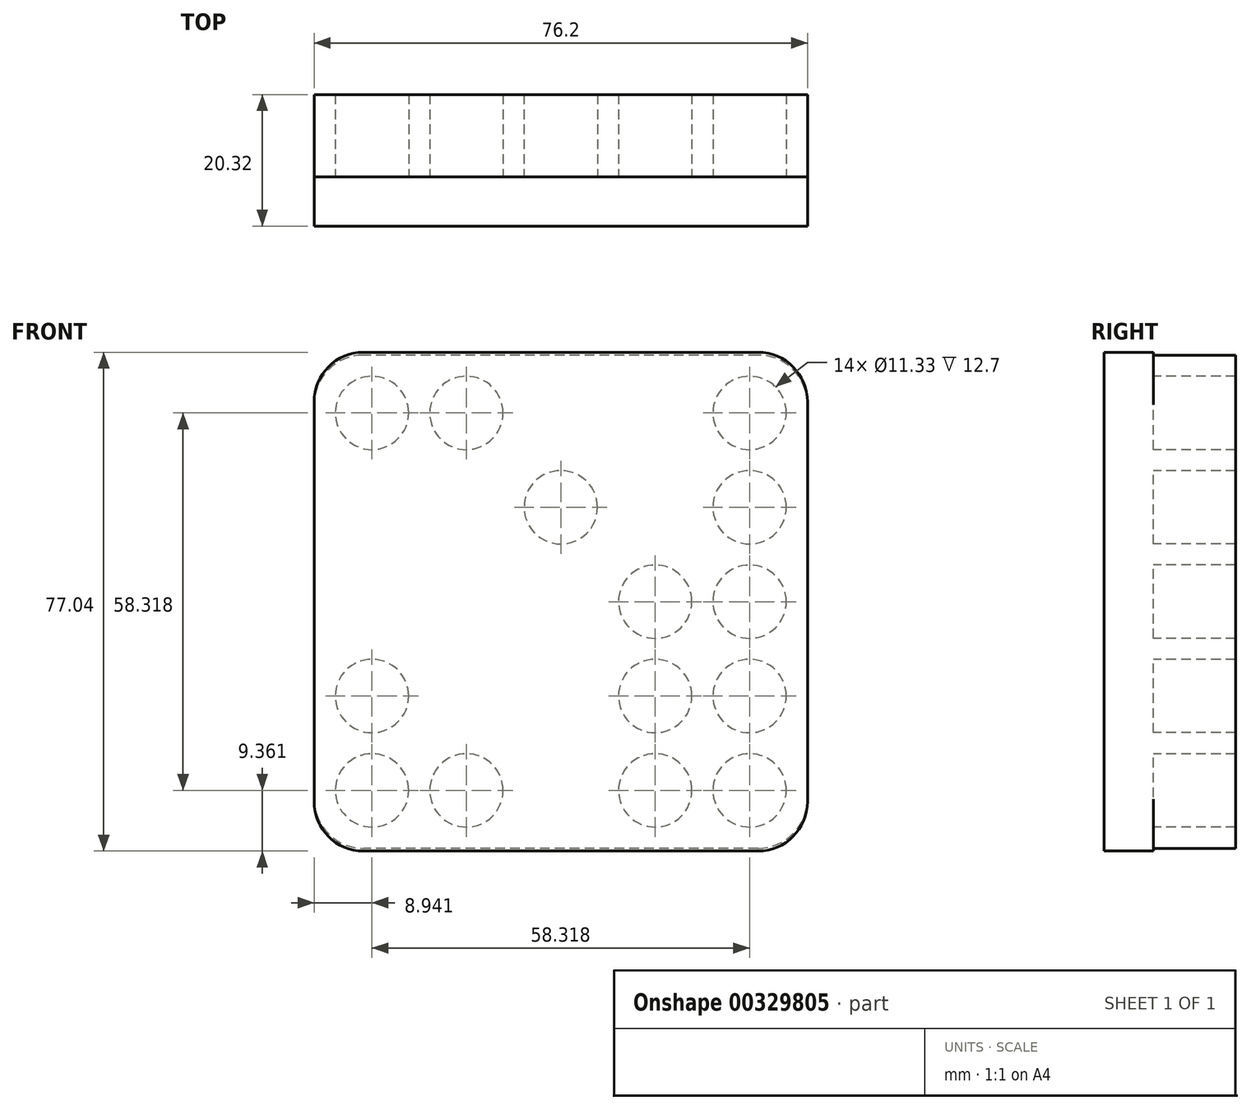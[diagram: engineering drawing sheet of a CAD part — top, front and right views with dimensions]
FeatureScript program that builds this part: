
annotation { "Feature Type Name" : "Feature", "Feature Type Description" : "" }
export const myFeature = defineFeature(function(context is Context, id is Id, definition is map)
    precondition{}
    {
        {
            var Q0;
            Q0=qCreatedBy(makeId("Front.planeOp"),FACE);
            var sketch = newSketch(context, id + "F0", { "sketchPlane" : qUnion([Q0])});
            skLineSegment(sketch, "E0.bottom", {"start": v(38.1, -38.1) * mm, "end": v(-38.1, -38.1) * mm});
            skLineSegment(sketch, "E0.top", {"start": v(38.1, 38.1) * mm, "end": v(-38.1, 38.1) * mm});
            skLineSegment(sketch, "E0.left", {"start": v(38.1, -38.1) * mm, "end": v(38.1, 38.1) * mm});
            skLineSegment(sketch, "E0.right", {"start": v(-38.1, -38.1) * mm, "end": v(-38.1, 38.1) * mm});
            skPoint(sketch, "E0.middle", {"position": v(0, 0) * mm});
            skLineSegment(sketch, "E1.left", {"start": v(38.1, -38.1) * mm, "end": v(38.1, -30.48) * mm});
            skSolve(sketch);
        }
        {
            var Q0;
            Q0 = qSketchRegion(id + "F0", true);
            extrude(context, id + "F1", {"entities" : qUnion([Q0]), "depth" : 12.7 * mm});
        }
        {
            var Q0;
            Q0=makeQuery(id+"F1.opExtrude","CAP_FACE",FACE,{"disambiguationData":[OSD([sQuery(id+"F0.wireOp",EDGE,"E0.bottom"),sQuery(id+"F0.wireOp",EDGE,"E0.top"),sQuery(id+"F0.wireOp",EDGE,"E0.left"),sQuery(id+"F0.wireOp",EDGE,"E0.right"),sQuery(id+"F0.wireOp",EDGE,"jwXeI2Gn-2uBu-UpR7-ZfaP-BlmGfNdsuJBv.bottom"),sQuery(id+"F0.wireOp",EDGE,"jwXeI2Gn-2uBu-UpR7-ZfaP-BlmGfNdsuJBv.top"),sQuery(id+"F0.wireOp",EDGE,"jwXeI2Gn-2uBu-UpR7-ZfaP-BlmGfNdsuJBv.right"),sQuery(id+"F0.wireOp",EDGE,"E1.bottom"),sQuery(id+"F0.wireOp",EDGE,"E1.top"),sQuery(id+"F0.wireOp",EDGE,"E1.right"),sQuery(id+"F0.wireOp",EDGE,"Ah4uGkzg-DGqc-S60Q-QTGu-lLs24q3gFamp.bottom"),sQuery(id+"F0.wireOp",EDGE,"Ah4uGkzg-DGqc-S60Q-QTGu-lLs24q3gFamp.left"),sQuery(id+"F0.wireOp",EDGE,"Ah4uGkzg-DGqc-S60Q-QTGu-lLs24q3gFamp.right")])],"isStart":false});
            var sketch = newSketch(context, id + "F2", { "sketchPlane" : qUnion([Q0])});
            skLineSegment(sketch, "E2.bottom", {"start": v(0, 0) * mm, "end": v(14.58, 0) * mm});
            skLineSegment(sketch, "E2.top", {"start": v(0, 14.58) * mm, "end": v(14.58, 14.58) * mm});
            skLineSegment(sketch, "E2.left", {"start": v(0, 0) * mm, "end": v(0, 14.58) * mm});
            skLineSegment(sketch, "E2.right", {"start": v(14.58, 0) * mm, "end": v(14.58, 14.58) * mm});
            skLineSegment(sketch, "E3.top", {"start": v(0, 29.16) * mm, "end": v(14.58, 29.16) * mm});
            skLineSegment(sketch, "E3.left", {"start": v(0, 14.58) * mm, "end": v(0, 29.16) * mm});
            skLineSegment(sketch, "E3.right", {"start": v(14.58, 14.58) * mm, "end": v(14.58, 29.16) * mm});
            skLineSegment(sketch, "E4.top", {"start": v(0, -14.58) * mm, "end": v(14.58, -14.58) * mm});
            skLineSegment(sketch, "E4.left", {"start": v(0, 0) * mm, "end": v(0, -14.58) * mm});
            skLineSegment(sketch, "E4.right", {"start": v(14.58, 0) * mm, "end": v(14.58, -14.58) * mm});
            skLineSegment(sketch, "E5.bottom", {"start": v(0, 0) * mm, "end": v(-14.58, 0) * mm});
            skLineSegment(sketch, "E5.top", {"start": v(0, -14.58) * mm, "end": v(-14.58, -14.58) * mm});
            skLineSegment(sketch, "E5.right", {"start": v(-14.58, 0) * mm, "end": v(-14.58, -14.58) * mm});
            skLineSegment(sketch, "E6.bottom", {"start": v(0, 14.58) * mm, "end": v(-14.58, 14.58) * mm});
            skLineSegment(sketch, "E6.left", {"start": v(0, 14.58) * mm, "end": v(0, 0) * mm});
            skLineSegment(sketch, "E6.right", {"start": v(-14.58, 14.58) * mm, "end": v(-14.58, 0) * mm});
            skLineSegment(sketch, "E7.top", {"start": v(0, 29.16) * mm, "end": v(-14.58, 29.16) * mm});
            skLineSegment(sketch, "E7.right", {"start": v(-14.58, 14.58) * mm, "end": v(-14.58, 29.16) * mm});
            skLineSegment(sketch, "E8.bottom", {"start": v(-14.58, 14.58) * mm, "end": v(-29.16, 14.58) * mm});
            skLineSegment(sketch, "E8.top", {"start": v(-14.58, 29.16) * mm, "end": v(-29.16, 29.16) * mm});
            skLineSegment(sketch, "E8.right", {"start": v(-29.16, 14.58) * mm, "end": v(-29.16, 29.16) * mm});
            skLineSegment(sketch, "E9.top", {"start": v(-14.58, 0) * mm, "end": v(-29.16, 0) * mm});
            skLineSegment(sketch, "E9.right", {"start": v(-29.16, 14.58) * mm, "end": v(-29.16, 0) * mm});
            skLineSegment(sketch, "E10.bottom", {"start": v(-14.58, -14.58) * mm, "end": v(-29.16, -14.58) * mm});
            skLineSegment(sketch, "E10.left", {"start": v(-14.58, -14.58) * mm, "end": v(-14.58, 0) * mm});
            skLineSegment(sketch, "E10.right", {"start": v(-29.16, -14.58) * mm, "end": v(-29.16, 0) * mm});
            skLineSegment(sketch, "E11.bottom", {"start": v(14.58, -14.58) * mm, "end": v(29.16, -14.58) * mm});
            skLineSegment(sketch, "E11.top", {"start": v(14.58, 0) * mm, "end": v(29.16, 0) * mm});
            skLineSegment(sketch, "E11.left", {"start": v(14.58, -14.58) * mm, "end": v(14.58, 0) * mm});
            skLineSegment(sketch, "E11.right", {"start": v(29.16, -14.58) * mm, "end": v(29.16, 0) * mm});
            skLineSegment(sketch, "E12.top", {"start": v(14.58, 14.58) * mm, "end": v(29.16, 14.58) * mm});
            skLineSegment(sketch, "E12.right", {"start": v(29.16, 0) * mm, "end": v(29.16, 14.58) * mm});
            skLineSegment(sketch, "E13.top", {"start": v(14.58, 29.16) * mm, "end": v(29.16, 29.16) * mm});
            skLineSegment(sketch, "E13.right", {"start": v(29.16, 14.58) * mm, "end": v(29.16, 29.16) * mm});
            skLineSegment(sketch, "E14.top", {"start": v(14.58, -29.16) * mm, "end": v(29.16, -29.16) * mm});
            skLineSegment(sketch, "E14.left", {"start": v(14.58, -14.58) * mm, "end": v(14.58, -29.16) * mm});
            skLineSegment(sketch, "E14.right", {"start": v(29.16, -14.58) * mm, "end": v(29.16, -29.16) * mm});
            skLineSegment(sketch, "E15.bottom", {"start": v(14.58, -29.16) * mm, "end": v(0, -29.16) * mm});
            skLineSegment(sketch, "E15.top", {"start": v(14.58, -14.58) * mm, "end": v(0, -14.58) * mm});
            skLineSegment(sketch, "E15.left", {"start": v(14.58, -29.16) * mm, "end": v(14.58, -14.58) * mm});
            skLineSegment(sketch, "E15.right", {"start": v(0, -29.16) * mm, "end": v(0, -14.58) * mm});
            skLineSegment(sketch, "E16.bottom", {"start": v(0, -29.16) * mm, "end": v(-14.58, -29.16) * mm});
            skLineSegment(sketch, "E16.right", {"start": v(-14.58, -29.16) * mm, "end": v(-14.58, -14.58) * mm});
            skLineSegment(sketch, "E17.bottom", {"start": v(-14.58, -29.16) * mm, "end": v(-29.16, -29.16) * mm});
            skLineSegment(sketch, "E17.right", {"start": v(-29.16, -29.16) * mm, "end": v(-29.16, -14.58) * mm});
            skSolve(sketch);
        }
        {
            var Q0;
            Q0=sQuery(id+"F2.wireOp",VERTEX,"E8.top.end");
            var Q1;
            Q1=sQuery(id+"F2.wireOp",VERTEX,"E8.top.start");
            var Q2;
            Q2=sQuery(id+"F2.wireOp",VERTEX,"E3.left.end");
            var Q3;
            Q3=sQuery(id+"F2.wireOp",VERTEX,"E3.right.end");
            var Q4;
            Q4=sQuery(id+"F2.wireOp",VERTEX,"E13.right.end");
            var Q5;
            Q5=sQuery(id+"F2.wireOp",VERTEX,"E12.top.end");
            var Q6;
            Q6=sQuery(id+"F2.wireOp",VERTEX,"E11.right.end");
            var Q7;
            Q7=sQuery(id+"F2.wireOp",VERTEX,"E11.bottom.end");
            var Q8;
            Q8=sQuery(id+"F2.wireOp",VERTEX,"E14.top.end");
            var Q9;
            Q9=sQuery(id+"F2.wireOp",VERTEX,"E14.top.start");
            var Q10;
            Q10=sQuery(id+"F2.wireOp",VERTEX,"E14.left.start");
            var Q11;
            Q11=sQuery(id+"F2.wireOp",VERTEX,"E11.left.end");
            var Q12;
            Q12=sQuery(id+"F2.wireOp",VERTEX,"E2.top.end");
            var Q13;
            Q13=sQuery(id+"F2.wireOp",VERTEX,"E6.left.start");
            var Q14;
            Q14=sQuery(id+"F2.wireOp",VERTEX,"E2.bottom.start");
            var Q15;
            Q15=sQuery(id+"F2.wireOp",VERTEX,"E4.left.end");
            var Q16;
            Q16=sQuery(id+"F2.wireOp",VERTEX,"E15.right.start");
            var Q17;
            Q17=sQuery(id+"F2.wireOp",VERTEX,"E16.right.start");
            var Q18;
            Q18=sQuery(id+"F2.wireOp",VERTEX,"E16.right.end");
            var Q19;
            Q19=sQuery(id+"F2.wireOp",VERTEX,"E6.right.end");
            var Q20;
            Q20=sQuery(id+"F2.wireOp",VERTEX,"E7.right.start");
            var Q21;
            Q21=sQuery(id+"F2.wireOp",VERTEX,"E8.bottom.end");
            var Q22;
            Q22=sQuery(id+"F2.wireOp",VERTEX,"E9.top.end");
            var Q23;
            Q23=sQuery(id+"F2.wireOp",VERTEX,"E17.right.end");
            var Q24;
            Q24=sQuery(id+"F2.wireOp",VERTEX,"E17.bottom.end");
            var Q25;
            Q25=makeQuery(id+"F1.opExtrude","SWEPT_BODY",BODY,{"disambiguationData":[OSD([sQuery(id+"F0.wireOp",EDGE,"E0.bottom"),sQuery(id+"F0.wireOp",EDGE,"E0.top"),sQuery(id+"F0.wireOp",EDGE,"E0.left"),sQuery(id+"F0.wireOp",EDGE,"E0.right"),sQuery(id+"F0.wireOp",EDGE,"jwXeI2Gn-2uBu-UpR7-ZfaP-BlmGfNdsuJBv.bottom"),sQuery(id+"F0.wireOp",EDGE,"jwXeI2Gn-2uBu-UpR7-ZfaP-BlmGfNdsuJBv.top"),sQuery(id+"F0.wireOp",EDGE,"jwXeI2Gn-2uBu-UpR7-ZfaP-BlmGfNdsuJBv.right"),sQuery(id+"F0.wireOp",EDGE,"E1.bottom"),sQuery(id+"F0.wireOp",EDGE,"E1.top"),sQuery(id+"F0.wireOp",EDGE,"E1.right"),sQuery(id+"F0.wireOp",EDGE,"Ah4uGkzg-DGqc-S60Q-QTGu-lLs24q3gFamp.bottom"),sQuery(id+"F0.wireOp",EDGE,"Ah4uGkzg-DGqc-S60Q-QTGu-lLs24q3gFamp.left"),sQuery(id+"F0.wireOp",EDGE,"Ah4uGkzg-DGqc-S60Q-QTGu-lLs24q3gFamp.right")])]});
            hole(context, id + "F3", {"style" : HoleStyle.SIMPLE, "endStyle" : HoleEndStyle.THROUGH, "holeDiameter" : 11.33 * mm, "tappedDepth" : 12.7 * mm, "tapClearance" : 3, "locations" : qUnion([Q0, Q1, Q2, Q3, Q4, Q5, Q6, Q7, Q8, Q9, Q10, Q11, Q12, Q13, Q14, Q15, Q16, Q17, Q18, Q19, Q20, Q21, Q22, Q23, Q24]), "scope" : qUnion([Q25])});
        }
        {
            var Q0;
            Q0=makeQuery(id+"F1.opExtrude","SWEPT_EDGE",EDGE,{"disambiguationData":[OSD([sQuery(id+"F0.wireOp",EDGE,"Ah4uGkzg-DGqc-S60Q-QTGu-lLs24q3gFamp.bottom"),sQuery(id+"F0.wireOp",EDGE,"Ah4uGkzg-DGqc-S60Q-QTGu-lLs24q3gFamp.right")])]});
            var Q1;
            Q1=makeQuery(id+"F1.opExtrude","SWEPT_EDGE",EDGE,{"disambiguationData":[OSD([sQuery(id+"F0.wireOp",EDGE,"Ah4uGkzg-DGqc-S60Q-QTGu-lLs24q3gFamp.bottom"),sQuery(id+"F0.wireOp",EDGE,"Ah4uGkzg-DGqc-S60Q-QTGu-lLs24q3gFamp.left")])]});
            var Q2;
            Q2=makeQuery(id+"F1.opExtrude","SWEPT_EDGE",EDGE,{"disambiguationData":[OSD([sQuery(id+"F0.wireOp",EDGE,"E0.top"),sQuery(id+"F0.wireOp",EDGE,"E0.right")])]});
            var Q3;
            Q3=makeQuery(id+"F1.opExtrude","SWEPT_EDGE",EDGE,{"disambiguationData":[OSD([sQuery(id+"F0.wireOp",EDGE,"E0.top"),sQuery(id+"F0.wireOp",EDGE,"E0.left")])]});
            var Q4;
            Q4=makeQuery(id+"F1.opExtrude","SWEPT_EDGE",EDGE,{"disambiguationData":[OSD([sQuery(id+"F0.wireOp",EDGE,"E1.top"),sQuery(id+"F0.wireOp",EDGE,"E1.right")])]});
            var Q5;
            Q5=makeQuery(id+"F1.opExtrude","SWEPT_EDGE",EDGE,{"disambiguationData":[OSD([sQuery(id+"F0.wireOp",EDGE,"jwXeI2Gn-2uBu-UpR7-ZfaP-BlmGfNdsuJBv.top"),sQuery(id+"F0.wireOp",EDGE,"jwXeI2Gn-2uBu-UpR7-ZfaP-BlmGfNdsuJBv.right")])]});
            var Q6;
            Q6=makeQuery(id+"F1.opExtrude","SWEPT_EDGE",EDGE,{"disambiguationData":[OSD([sQuery(id+"F0.wireOp",EDGE,"E0.bottom"),sQuery(id+"F0.wireOp",EDGE,"E1.left")])]});
            var Q7;
            Q7=makeQuery(id+"F1.opExtrude","SWEPT_EDGE",EDGE,{"disambiguationData":[OSD([sQuery(id+"F0.wireOp",EDGE,"E0.bottom"),sQuery(id+"F0.wireOp",EDGE,"E0.right")])]});
            fillet(context, id + "F4", {"entities" : qUnion([Q0, Q1, Q2, Q3, Q4, Q5, Q6, Q7]), "radius" : 7.62 * mm, "tangentPropagation" : true, "allowEdgeOverflow" : false});
        }
        {
            var Q0;
            Q0=makeQuery(id+"F1.opExtrude","CAP_FACE",FACE,{"disambiguationData":[OSD([sQuery(id+"F0.wireOp",EDGE,"E0.bottom"),sQuery(id+"F0.wireOp",EDGE,"E0.top"),sQuery(id+"F0.wireOp",EDGE,"E0.left"),sQuery(id+"F0.wireOp",EDGE,"E0.right"),sQuery(id+"F0.wireOp",EDGE,"E1.left")])],"isStart":false});
            var sketch = newSketch(context, id + "F5", { "sketchPlane" : qUnion([Q0])});
            skLineSegment(sketch, "E18.bottom", {"start": v(38.1, -38.52) * mm, "end": v(-38.1, -38.52) * mm});
            skLineSegment(sketch, "E18.top", {"start": v(38.1, 38.52) * mm, "end": v(-38.1, 38.52) * mm});
            skLineSegment(sketch, "E18.left", {"start": v(38.1, -38.52) * mm, "end": v(38.1, 38.52) * mm});
            skLineSegment(sketch, "E18.right", {"start": v(-38.1, -38.52) * mm, "end": v(-38.1, 38.52) * mm});
            skPoint(sketch, "E18.middle", {"position": v(0, 0) * mm});
            skSolve(sketch);
        }
        {
            var Q0;
            Q0 = qSketchRegion(id + "F5", true);
            extrude(context, id + "F6", {"entities" : qUnion([Q0]), "operationType" : NewBodyOperationType.ADD, "depth" : 7.62 * mm});
        }
        {
            var Q0;
            Q0=makeQuery(id+"F6.opExtrude","SWEPT_EDGE",EDGE,{"disambiguationData":[OSD([sQuery(id+"F5.wireOp",EDGE,"E18.top"),sQuery(id+"F5.wireOp",EDGE,"E18.right")])]});
            var Q1;
            Q1=makeQuery(id+"F6.opExtrude","SWEPT_EDGE",EDGE,{"disambiguationData":[OSD([sQuery(id+"F5.wireOp",EDGE,"E18.top"),sQuery(id+"F5.wireOp",EDGE,"E18.left")])]});
            var Q2;
            Q2=makeQuery(id+"F6.opExtrude","SWEPT_EDGE",EDGE,{"disambiguationData":[OSD([sQuery(id+"F5.wireOp",EDGE,"E18.bottom"),sQuery(id+"F5.wireOp",EDGE,"E18.left")])]});
            var Q3;
            Q3=makeQuery(id+"F6.opExtrude","SWEPT_EDGE",EDGE,{"disambiguationData":[OSD([sQuery(id+"F5.wireOp",EDGE,"E18.bottom"),sQuery(id+"F5.wireOp",EDGE,"E18.right")])]});
            fillet(context, id + "F7", {"entities" : qUnion([Q0, Q1, Q2, Q3]), "radius" : 7.62 * mm, "tangentPropagation" : true, "allowEdgeOverflow" : false});
        }
    });
